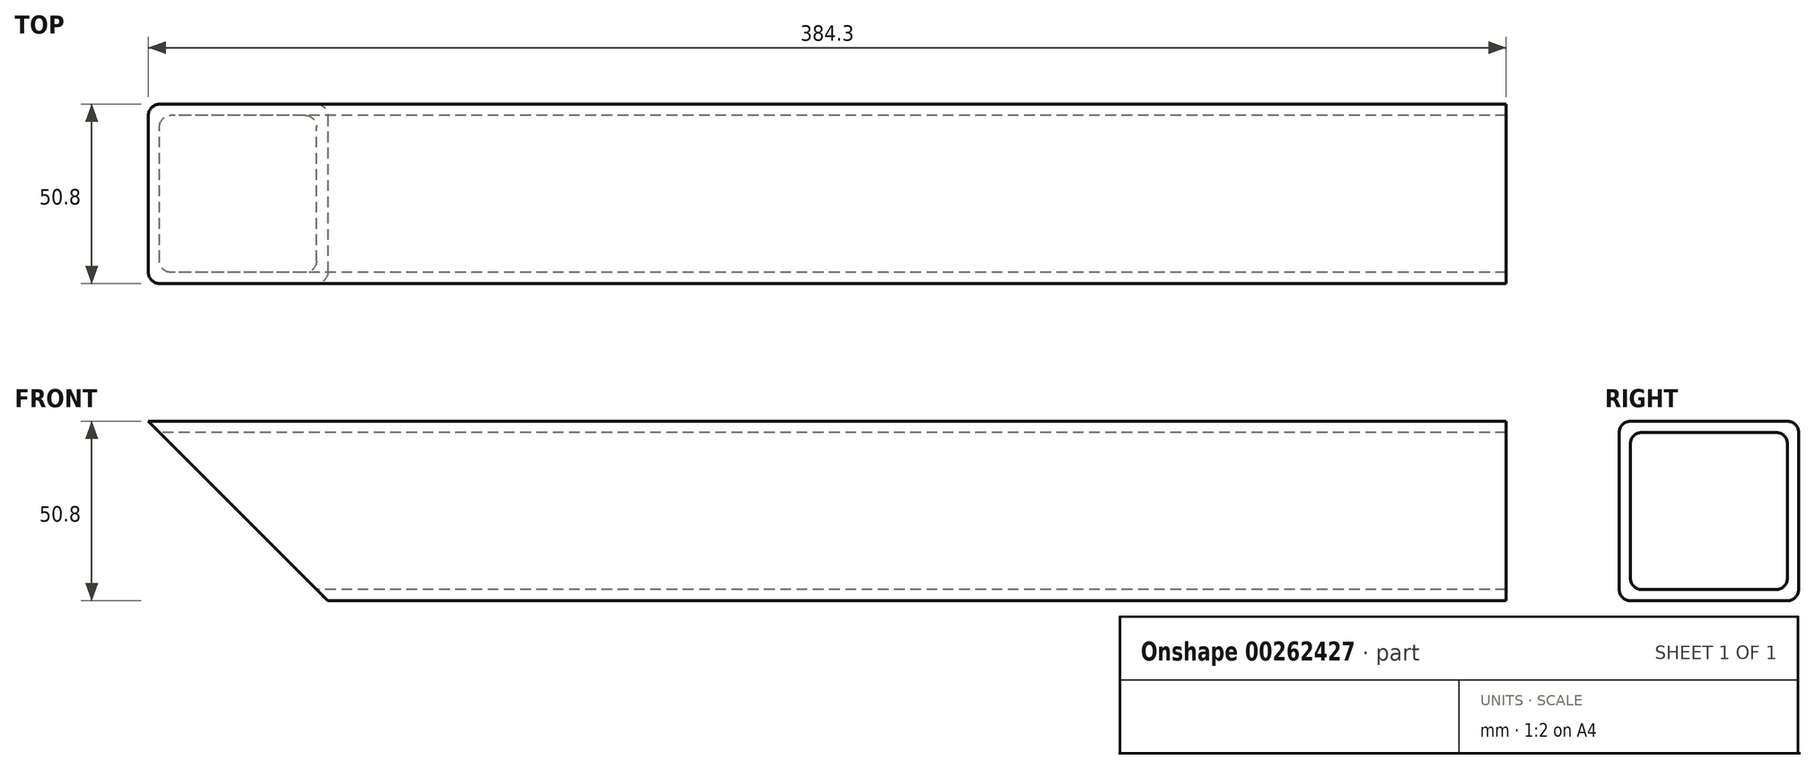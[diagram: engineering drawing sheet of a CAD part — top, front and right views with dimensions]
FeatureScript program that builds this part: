
annotation { "Feature Type Name" : "Feature", "Feature Type Description" : "" }
export const myFeature = defineFeature(function(context is Context, id is Id, definition is map)
    precondition{}
    {
        {
            var Q0;
            Q0=qCreatedBy(makeId("Right.planeOp"),FACE);
            var sketch = newSketch(context, id + "F0", { "sketchPlane" : qUnion([Q0])});
            skLineSegment(sketch, "E0.bottom", {"start": v(22.23, 25.4) * mm, "end": v(-22.23, 25.4) * mm});
            skLineSegment(sketch, "E0.top", {"start": v(22.23, -25.4) * mm, "end": v(-22.23, -25.4) * mm});
            skLineSegment(sketch, "E0.left", {"start": v(25.4, 22.23) * mm, "end": v(25.4, -22.23) * mm});
            skLineSegment(sketch, "E0.right", {"start": v(-25.4, 22.23) * mm, "end": v(-25.4, -22.23) * mm});
            skPoint(sketch, "E0.middle", {"position": v(0, 0) * mm});
            skLineSegment(sketch, "E1.bottom", {"start": v(19.05, 22.23) * mm, "end": v(-19.05, 22.23) * mm});
            skLineSegment(sketch, "E1.top", {"start": v(19.05, -22.23) * mm, "end": v(-19.05, -22.23) * mm});
            skLineSegment(sketch, "E1.left", {"start": v(22.22, 19.05) * mm, "end": v(22.22, -19.05) * mm});
            skLineSegment(sketch, "E1.right", {"start": v(-22.22, 19.05) * mm, "end": v(-22.22, -19.05) * mm});
            skPoint(sketch, "E2.visualSharp", {"position": v(-22.23, 22.23) * mm});
            skArc(sketch, "E2.filletArc", {"start": v(-19.05, 22.23) * mm, "mid": v(-21.3, 21.3) * mm, "end": v(-22.22, 19.05) * mm});
            skPoint(sketch, "E3.visualSharp", {"position": v(-25.4, 25.4) * mm});
            skArc(sketch, "E3.filletArc", {"start": v(-22.23, 25.4) * mm, "mid": v(-24.47, 24.47) * mm, "end": v(-25.4, 22.23) * mm});
            skPoint(sketch, "E4.visualSharp", {"position": v(-22.23, -22.23) * mm});
            skArc(sketch, "E4.filletArc", {"start": v(-22.22, -19.05) * mm, "mid": v(-21.3, -21.3) * mm, "end": v(-19.05, -22.23) * mm});
            skPoint(sketch, "E5.visualSharp", {"position": v(-25.4, -25.4) * mm});
            skArc(sketch, "E5.filletArc", {"start": v(-25.4, -22.23) * mm, "mid": v(-24.47, -24.47) * mm, "end": v(-22.23, -25.4) * mm});
            skPoint(sketch, "E6.visualSharp", {"position": v(22.23, -22.23) * mm});
            skArc(sketch, "E6.filletArc", {"start": v(19.05, -22.23) * mm, "mid": v(21.3, -21.3) * mm, "end": v(22.22, -19.05) * mm});
            skPoint(sketch, "E7.visualSharp", {"position": v(25.4, -25.4) * mm});
            skArc(sketch, "E7.filletArc", {"start": v(22.23, -25.4) * mm, "mid": v(24.47, -24.47) * mm, "end": v(25.4, -22.23) * mm});
            skPoint(sketch, "E8.visualSharp", {"position": v(22.23, 22.23) * mm});
            skArc(sketch, "E8.filletArc", {"start": v(22.22, 19.05) * mm, "mid": v(21.3, 21.3) * mm, "end": v(19.05, 22.22) * mm});
            skPoint(sketch, "E9.visualSharp", {"position": v(25.4, 25.4) * mm});
            skArc(sketch, "E9.filletArc", {"start": v(25.4, 22.23) * mm, "mid": v(24.47, 24.47) * mm, "end": v(22.23, 25.4) * mm});
            skSolve(sketch);
        }
        {
            var Q0;
            Q0 = qSketchRegion(id + "F0", true);
            extrude(context, id + "F1", {"entities" : qUnion([Q0]), "depth" : 384.3 * mm});
        }
        {
            var Q0;
            Q0=qCreatedBy(makeId("Front.planeOp"),FACE);
            var sketch = newSketch(context, id + "F2", { "sketchPlane" : qUnion([Q0])});
            skLineSegment(sketch, "E10.top", {"start": v(50.8, -25.4) * mm, "end": v(0, -25.4) * mm});
            skLineSegment(sketch, "E10.right", {"start": v(0, 25.4) * mm, "end": v(0, -25.4) * mm});
            skPoint(sketch, "E10.middle", {"position": v(25.4, 0) * mm});
            skLineSegment(sketch, "E11", {"start": v(0, 25.4) * mm, "end": v(50.8, -25.4) * mm});
            skPoint(sketch, "E10.left.start.orphan", {"position": v(50.8, 25.4) * mm});
            skSolve(sketch);
        }
        {
            var Q0;
            Q0 = qSketchRegion(id + "F2", true);
            extrude(context, id + "F3", {"entities" : qUnion([Q0]), "operationType" : NewBodyOperationType.REMOVE, "oppositeDirection" : true, "depth" : 25.4 * mm, "hasSecondDirection" : true, "secondDirectionOppositeDirection" : false, "secondDirectionDepth" : 25.4 * mm});
        }
    });
